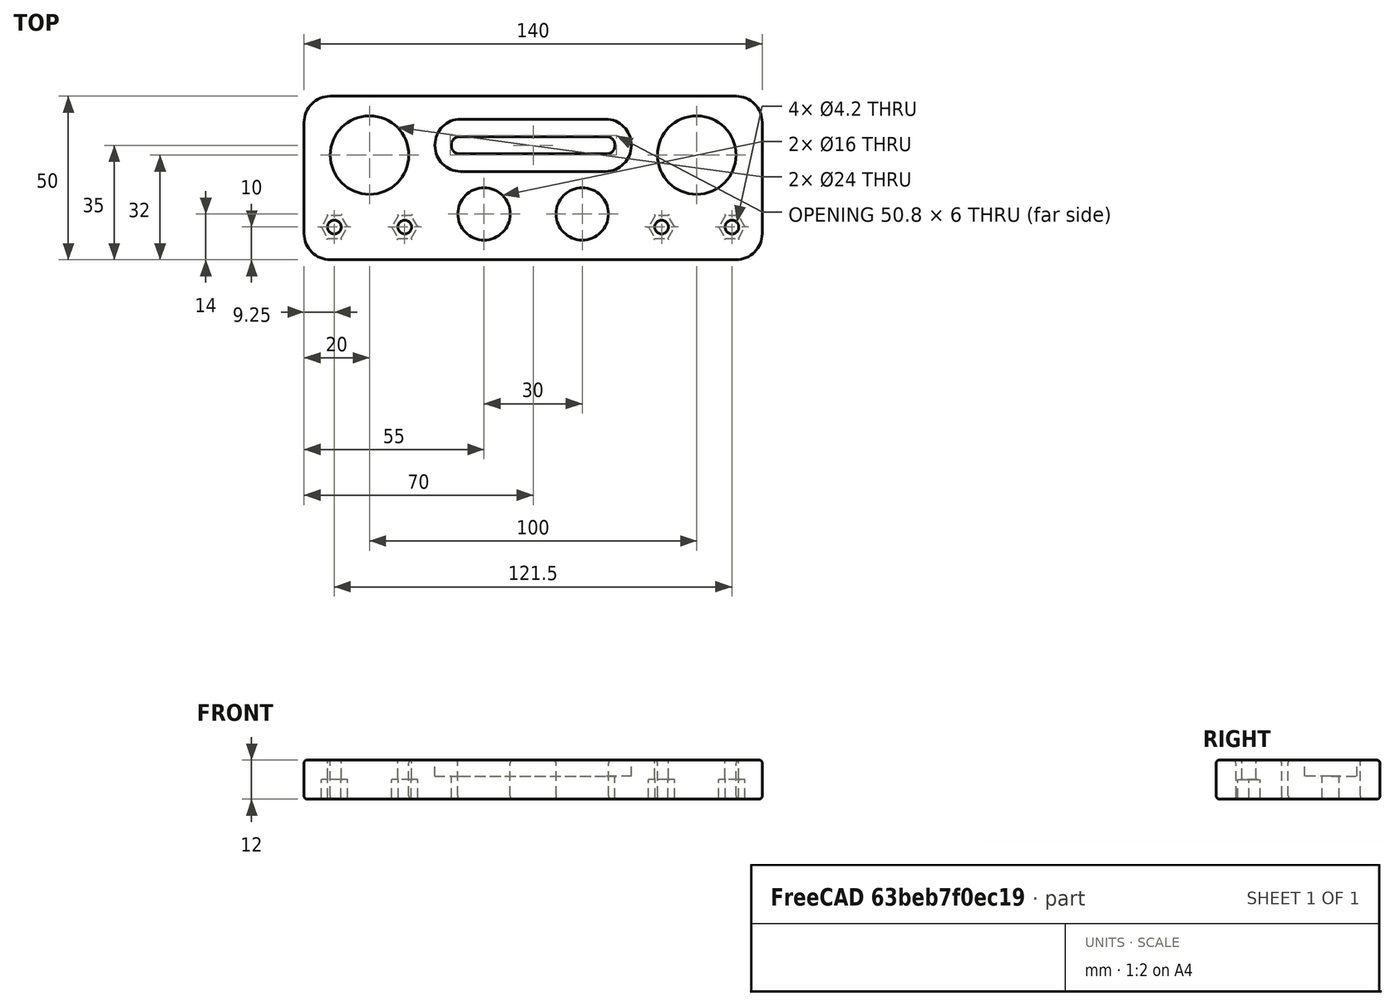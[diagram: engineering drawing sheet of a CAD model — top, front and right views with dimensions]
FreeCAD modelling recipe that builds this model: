
FCSTD DOCUMENT  (FreeCAD 0.18R16146 (Git))
Label: X_Grundplatte_Mitte_Ver2
License: All rights reserved
LicenseURL: http://en.wikipedia.org/wiki/All_rights_reserved
objects: Part::Cut×14, Part::Cylinder×8, Part::Fillet×5, Part::Part2DObjectPython×4, Part::Extrusion×4, Part::Box×3
note: 38 computed .brp shape members not serialized (recipe doc carries the construction recipe); baked Part::Feature solids carry a one-line shape summary decoded from their .brp

FEATURE [Part::Box] Box  label="Würfel"
  AttacherType = Attacher::AttachEngine3D
  Height = 12
  Length = 140
  Width = 50
FEATURE [Part::Cylinder] Cylinder007  label="Bohrung002"
  Angle = 360
  AttacherType = Attacher::AttachEngine3D
  Height = 20
  Placement = pos=(9.25,10,0) rot=(0,0,1;0rad)
  Radius = 2.1
FEATURE [Part::Cylinder] Cylinder009  label="Bohrung004"
  Angle = 360
  AttacherType = Attacher::AttachEngine3D
  Height = 20
  Placement = pos=(30.75,10,0) rot=(0,0,1;0rad)
  Radius = 2.1
FEATURE [Part::Cylinder] Cylinder010  label="Bohrung005"
  Angle = 360
  AttacherType = Attacher::AttachEngine3D
  Height = 20
  Placement = pos=(130.75,10,0) rot=(0,0,1;0rad)
  Radius = 2.1
FEATURE [Part::Cylinder] Cylinder011  label="Bohrung006"
  Angle = 360
  AttacherType = Attacher::AttachEngine3D
  Height = 20
  Placement = pos=(109.25,10,0) rot=(0,0,1;0rad)
  Radius = 2.1
FEATURE [Part::Part2DObjectPython] Polygon001  # Draft 2D object (typed FeaturePython)
  ChamferSize = 0
  DrawMode = 0
  FacesNumber = 6
  FilletRadius = 0
  MakeFace = true
  Radius = 4
FEATURE [Part::Extrusion] Extrude001  label="Mutter002"
  Base = -> Polygon001
  Dir = (0,0,1)
  DirMode = 2
  FaceMakerClass = Part::FaceMakerBullseye
  LengthFwd = 6
  LengthRev = 0
  Placement = pos=(9.25,10,0) rot=(0,0,1;0rad)
  Solid = false
  Symmetric = false
FEATURE [Part::Part2DObjectPython] Polygon003  # Draft 2D object (typed FeaturePython)
  ChamferSize = 0
  DrawMode = 0
  FacesNumber = 6
  FilletRadius = 0
  MakeFace = true
  Radius = 4
FEATURE [Part::Extrusion] Extrude003  label="Mutter004"
  Base = -> Polygon003
  Dir = (0,0,1)
  DirMode = 2
  FaceMakerClass = Part::FaceMakerBullseye
  LengthFwd = 6
  LengthRev = 0
  Placement = pos=(30.75,10,0) rot=(0,0,1;0rad)
  Solid = false
  Symmetric = false
FEATURE [Part::Part2DObjectPython] Polygon005  # Draft 2D object (typed FeaturePython)
  ChamferSize = 0
  DrawMode = 0
  FacesNumber = 6
  FilletRadius = 0
  MakeFace = true
  Radius = 4
FEATURE [Part::Extrusion] Extrude005  label="Mutter006"
  Base = -> Polygon005
  Dir = (0,0,1)
  DirMode = 2
  FaceMakerClass = Part::FaceMakerBullseye
  LengthFwd = 6
  LengthRev = 0
  Placement = pos=(130.75,10,0) rot=(0,0,1;0rad)
  Solid = false
  Symmetric = false
FEATURE [Part::Part2DObjectPython] Polygon006  # Draft 2D object (typed FeaturePython)
  ChamferSize = 0
  DrawMode = 0
  FacesNumber = 6
  FilletRadius = 0
  MakeFace = true
  Radius = 4
FEATURE [Part::Extrusion] Extrude006  label="Mutter007"
  Base = -> Polygon006
  Dir = (0,0,1)
  DirMode = 2
  FaceMakerClass = Part::FaceMakerBullseye
  LengthFwd = 6
  LengthRev = 0
  Placement = pos=(109.25,10,0) rot=(0,0,1;0rad)
  Solid = false
  Symmetric = false
FEATURE [Part::Box] Box013  label="Würfel013"
  AttacherType = Attacher::AttachEngine3D
  Height = 20
  Length = 60
  Placement = pos=(40,27,7) rot=(0,0,1;0rad)
  Width = 16
FEATURE [Part::Fillet] Fillet004
  Base = -> Box013
  Edges = 4 edges r=7.9: [Edge1,Edge3,Edge5,Edge7]
FEATURE [Part::Box] Box014  label="Würfel014"
  AttacherType = Attacher::AttachEngine3D
  Height = 20
  Length = 50
  Placement = pos=(45,32.4,0) rot=(0,0,1;0rad)
  Width = 5.2
FEATURE [Part::Fillet] Fillet005
  Base = -> Box014
  Edges = 4 edges r=2.5: [Edge1,Edge3,Edge5,Edge7]
FEATURE [Part::Cylinder] Cylinder
  Angle = 360
  AttacherType = Attacher::AttachEngine3D
  Height = 30
  Placement = pos=(20,32,0) rot=(0,0,1;0rad)
  Radius = 12
FEATURE [Part::Cylinder] Cylinder012
  Angle = 360
  AttacherType = Attacher::AttachEngine3D
  Height = 30
  Placement = pos=(120,32,0) rot=(0,0,1;0rad)
  Radius = 12
FEATURE [Part::Cylinder] Cylinder013
  Angle = 360
  AttacherType = Attacher::AttachEngine3D
  Height = 30
  Placement = pos=(55,14,0) rot=(0,0,1;0rad)
  Radius = 8
FEATURE [Part::Cylinder] Cylinder014
  Angle = 360
  AttacherType = Attacher::AttachEngine3D
  Height = 30
  Placement = pos=(85,14,0) rot=(0,0,1;0rad)
  Radius = 8
FEATURE [Part::Cut] Cut
  Base = -> Box
  Tool = -> Fillet004
FEATURE [Part::Cut] Cut001
  Base = -> Cut
  Tool = -> Fillet005
FEATURE [Part::Cut] Cut002
  Base = -> Cut001
  Tool = -> Extrude001
FEATURE [Part::Cut] Cut003
  Base = -> Cut002
  Tool = -> Extrude003
FEATURE [Part::Cut] Cut004
  Base = -> Cut003
  Tool = -> Extrude005
FEATURE [Part::Cut] Cut005
  Base = -> Cut004
  Tool = -> Extrude006
FEATURE [Part::Cut] Cut006
  Base = -> Cut005
  Tool = -> Cylinder007
FEATURE [Part::Cut] Cut007
  Base = -> Cut006
  Tool = -> Cylinder009
FEATURE [Part::Cut] Cut008
  Base = -> Cut007
  Tool = -> Cylinder010
FEATURE [Part::Cut] Cut009
  Base = -> Cut008
  Tool = -> Cylinder011
FEATURE [Part::Cut] Cut010
  Base = -> Cut009
  Tool = -> Cylinder
FEATURE [Part::Cut] Cut011
  Base = -> Cut010
  Tool = -> Cylinder012
FEATURE [Part::Cut] Cut012
  Base = -> Cut011
  Tool = -> Cylinder013
FEATURE [Part::Cut] Cut013
  Base = -> Cut012
  Tool = -> Cylinder014
FEATURE [Part::Fillet] Fillet
  Base = -> Cut013
  Edges = 4 edges r=8: [Edge1,Edge3,Edge6,Edge27]
FEATURE [Part::Fillet] Fillet006
  Base = -> Fillet
  Edges = 24 edges r=1: [Edge1,Edge4,Edge5,Edge6,Edge7,Edge8,Edge9,Edge10,Edge11,Edge12,Edge13,Edge22,Edge25,Edge28,Edge30,Edge32,Edge33,Edge34,Edge35,Edge36,Edge37,Edge38,Edge47,Edge60]
FEATURE [Part::Fillet] Fillet007
  Base = -> Fillet006
  Edges = 50 edges r=0.4: [Edge30,Edge32,Edge33,Edge34,Edge35,Edge37,Edge38,Edge39,Edge40,Edge41,Edge42,Edge43,Edge44,Edge45,Edge46,Edge47,Edge48,Edge49,Edge50,Edge51,Edge52,Edge53,Edge54,Edge55,Edge56,Edge57,Edge58,Edge59,Edge60,Edge61,Edge73,Edge75,Edge76,Edge77,Edge78,Edge80,Edge81,Edge82,Edge83,Edge84,Edge104,Edge109,+8 more]
